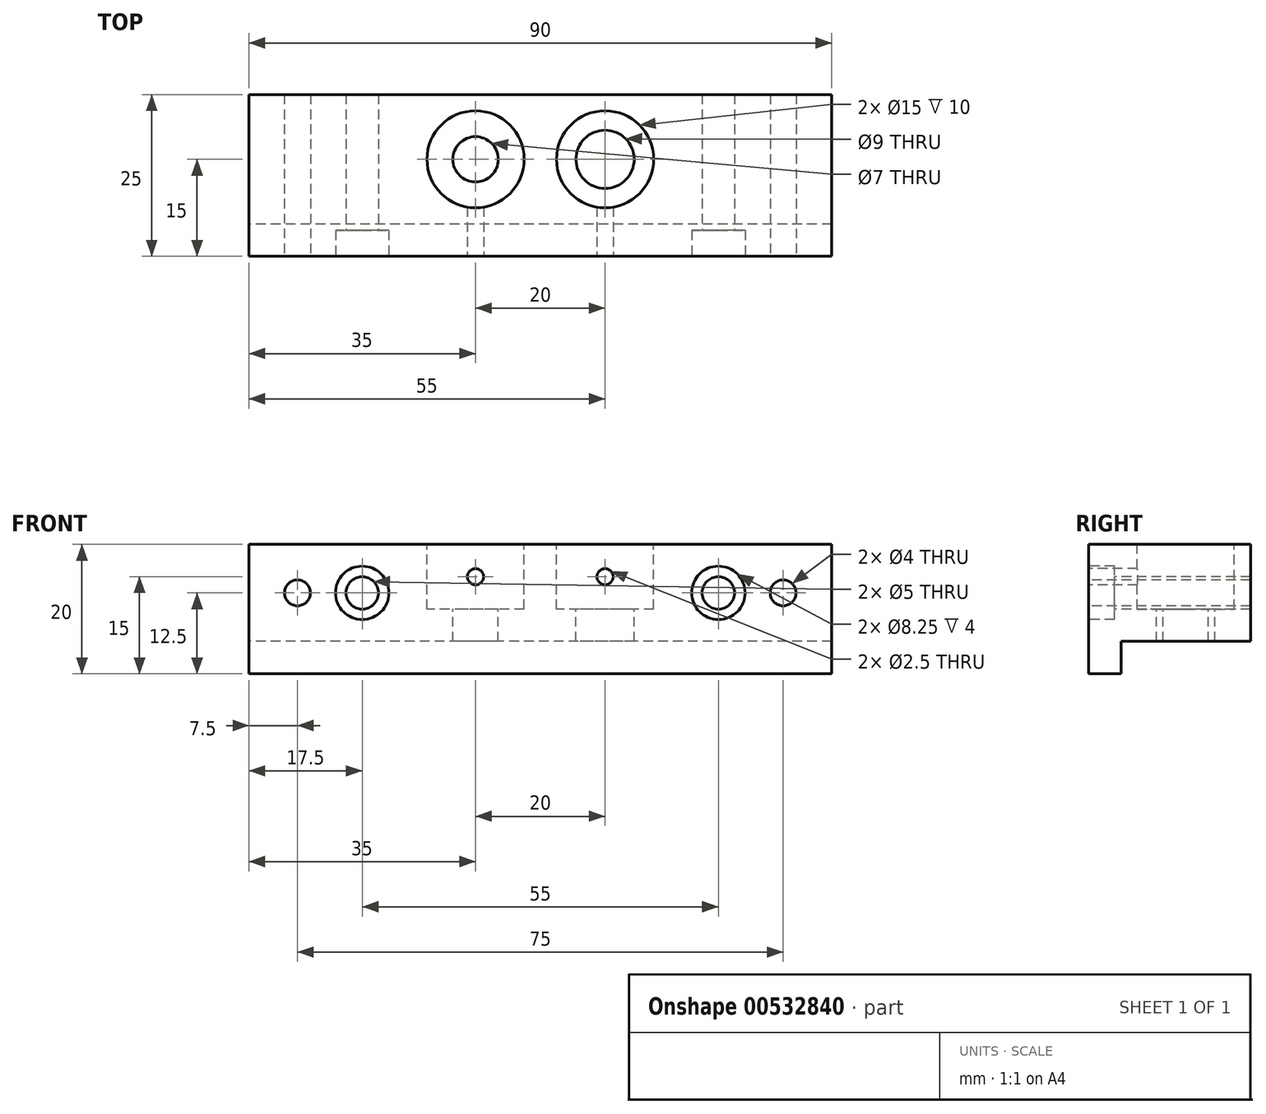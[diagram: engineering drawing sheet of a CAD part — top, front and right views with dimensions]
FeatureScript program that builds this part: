
annotation { "Feature Type Name" : "Feature", "Feature Type Description" : "" }
export const myFeature = defineFeature(function(context is Context, id is Id, definition is map)
    precondition{}
    {
        {
            var Q0;
            Q0=qCreatedBy(makeId("Right.planeOp"),FACE);
            var sketch = newSketch(context, id + "F0", { "sketchPlane" : qUnion([Q0])});
            skLineSegment(sketch, "E0", {"start": v(-25, 0) * mm, "end": v(-25, 20) * mm});
            skLineSegment(sketch, "E1", {"start": v(-25, 20) * mm, "end": v(0, 20) * mm});
            skLineSegment(sketch, "E2", {"start": v(0, 20) * mm, "end": v(0, 5) * mm});
            skLineSegment(sketch, "E3", {"start": v(0, 5) * mm, "end": v(-20, 5) * mm});
            skLineSegment(sketch, "E4", {"start": v(-20, 5) * mm, "end": v(-20, 0) * mm});
            skLineSegment(sketch, "E5", {"start": v(-20, 0) * mm, "end": v(-25, 0) * mm});
            skSolve(sketch);
        }
        {
            var Q0;
            Q0 = qSketchRegion(id + "F0", true);
            extrude(context, id + "F1", {"entities" : qUnion([Q0]), "endBound" : BoundingType.SYMMETRIC, "depth" : 90 * mm, "offsetDistance" : 25 * mm});
        }
        {
            var Q0;
            Q0=makeQuery(id+"F1.opExtrude","SWEPT_FACE",FACE,{"disambiguationData":[OSD([sQuery(id+"F0.wireOp",EDGE,"E0")])]});
            var sketch = newSketch(context, id + "F2", { "sketchPlane" : qUnion([Q0])});
            skPoint(sketch, "E6", {"position": v(-27.5, 12.5) * mm});
            skPoint(sketch, "E7", {"position": v(27.5, 12.5) * mm});
            skCircle(sketch, "E8", {"center": v(-37.5, 12.5) * mm, "radius": 2 * mm});
            skCircle(sketch, "E9", {"center": v(37.5, 12.5) * mm, "radius": 2 * mm});
            skSolve(sketch);
        }
        {
            var Q0;
            Q0=makeQuery(id+"F2.imprint","IMPRINT",FACE,{"disambiguationData":[TD([[makeQuery(id+"F2.imprint","IMPRINT",EDGE,{"derivedFrom":sQuery(id+"F2.wireOp",EDGE,"E8")}),1.0]])]});
            var Q1;
            Q1=makeQuery(id+"F2.imprint","IMPRINT",FACE,{"disambiguationData":[TD([[makeQuery(id+"F2.imprint","IMPRINT",EDGE,{"derivedFrom":sQuery(id+"F2.wireOp",EDGE,"E9")}),1.0]])]});
            extrude(context, id + "F3", {"entities" : qUnion([Q0, Q1]), "operationType" : NewBodyOperationType.REMOVE, "endBound" : BoundingType.THROUGH_ALL, "oppositeDirection" : true, "depth" : 25 * mm, "offsetDistance" : 25 * mm});
        }
        {
            var Q0;
            Q0=sQuery(id+"F2.wireOp",VERTEX,"E6");
            var Q1;
            Q1=sQuery(id+"F2.wireOp",VERTEX,"E7");
            var Q2;
            Q2=makeQuery(id+"F1.opExtrude","SWEPT_BODY",BODY,{"disambiguationData":[OSD([sQuery(id+"F0.wireOp",EDGE,"E0"),sQuery(id+"F0.wireOp",EDGE,"E1"),sQuery(id+"F0.wireOp",EDGE,"E2"),sQuery(id+"F0.wireOp",EDGE,"E3"),sQuery(id+"F0.wireOp",EDGE,"E4"),sQuery(id+"F0.wireOp",EDGE,"E5")])]});
            hole(context, id + "F4", {"style" : HoleStyle.C_BORE, "endStyle" : HoleEndStyle.THROUGH, "standardTappedOrClearance" : lookupTablePath({ "standard" : "ISO", "size" : "5", "type" : "Drilled" }), "standardBlindInLast" : lookupTablePath({ "standard" : "ISO", "size" : "5", "type" : "Drilled" }), "holeDiameter" : 5 * mm, "cBoreDiameter" : 8.25 * mm, "cBoreDepth" : 4 * mm, "isTappedThrough" : true, "tappedDepth" : 10.9 * mm, "tapClearance" : 3, "locations" : qUnion([Q0, Q1]), "scope" : qUnion([Q2])});
        }
        {
            var Q0;
            Q0=makeQuery(id+"F1.opExtrude","SWEPT_FACE",FACE,{"disambiguationData":[OSD([sQuery(id+"F0.wireOp",EDGE,"E1")])]});
            var sketch = newSketch(context, id + "F5", { "sketchPlane" : qUnion([Q0])});
            skCircle(sketch, "E10", {"center": v(-10, -10) * mm, "radius": 7.5 * mm});
            skCircle(sketch, "E11", {"center": v(-10, -10) * mm, "radius": 3.5 * mm});
            skCircle(sketch, "E12", {"center": v(10, -10) * mm, "radius": 7.5 * mm});
            skCircle(sketch, "E13", {"center": v(10, -10) * mm, "radius": 4.5 * mm});
            skSolve(sketch);
        }
        {
            var Q0;
            Q0=makeQuery(id+"F5.imprint","IMPRINT",FACE,{"disambiguationData":[TD([[makeQuery(id+"F5.imprint","IMPRINT",EDGE,{"derivedFrom":sQuery(id+"F5.wireOp",EDGE,"E11")}),1.0]])]});
            var Q1;
            Q1=makeQuery(id+"F5.imprint","IMPRINT",FACE,{"disambiguationData":[TD([[makeQuery(id+"F5.imprint","IMPRINT",EDGE,{"derivedFrom":sQuery(id+"F5.wireOp",EDGE,"E13")}),1.0]])]});
            extrude(context, id + "F6", {"entities" : qUnion([Q0, Q1]), "operationType" : NewBodyOperationType.REMOVE, "endBound" : BoundingType.THROUGH_ALL, "oppositeDirection" : true, "depth" : 25 * mm, "offsetDistance" : 25 * mm});
        }
        {
            var Q0;
            Q0=makeQuery(id+"F5.imprint","IMPRINT",FACE,{"disambiguationData":[TD([[makeQuery(id+"F5.imprint","IMPRINT",EDGE,{"derivedFrom":sQuery(id+"F5.wireOp",EDGE,"E10")}),1.0]])]});
            var Q1;
            Q1=makeQuery(id+"F5.imprint","IMPRINT",FACE,{"disambiguationData":[TD([[makeQuery(id+"F5.imprint","IMPRINT",EDGE,{"derivedFrom":sQuery(id+"F5.wireOp",EDGE,"E12")}),1.0]])]});
            extrude(context, id + "F7", {"entities" : qUnion([Q0, Q1]), "operationType" : NewBodyOperationType.REMOVE, "oppositeDirection" : true, "depth" : 10 * mm, "offsetDistance" : 25 * mm});
        }
        {
            var Q0;
            Q0=makeQuery(id+"F1.opExtrude","SWEPT_FACE",FACE,{"disambiguationData":[OSD([sQuery(id+"F0.wireOp",EDGE,"E0")])]});
            var sketch = newSketch(context, id + "F8", { "sketchPlane" : qUnion([Q0])});
            skPoint(sketch, "E14", {"position": v(-10, 15) * mm});
            skPoint(sketch, "E15", {"position": v(10, 15) * mm});
            skSolve(sketch);
        }
        {
            var Q0;
            Q0=sQuery(id+"F8.wireOp",VERTEX,"E14");
            var Q1;
            Q1=sQuery(id+"F8.wireOp",VERTEX,"E15");
            var Q2;
            Q2=makeQuery(id+"F1.opExtrude","SWEPT_BODY",BODY,{"disambiguationData":[OSD([sQuery(id+"F0.wireOp",EDGE,"E0"),sQuery(id+"F0.wireOp",EDGE,"E1"),sQuery(id+"F0.wireOp",EDGE,"E2"),sQuery(id+"F0.wireOp",EDGE,"E3"),sQuery(id+"F0.wireOp",EDGE,"E4"),sQuery(id+"F0.wireOp",EDGE,"E5")])]});
            hole(context, id + "F9", {"style" : HoleStyle.SIMPLE, "endStyle" : HoleEndStyle.BLIND, "standardTappedOrClearance" : lookupTablePath({ "standard" : "ISO", "engagement" : "75%", "pitch" : "0.5 mm", "size" : "M3", "type" : "Tapped" }), "standardBlindInLast" : lookupTablePath({ "standard" : "ISO", "engagement" : "75%", "pitch" : "0.5 mm", "size" : "M3", "type" : "Tapped" }), "holeDiameter" : 2.5 * mm, "showTappedDepth" : true, "holeDepth" : 12.4 * mm, "isTappedThrough" : true, "tappedDepth" : 10.9 * mm, "tapClearance" : 3, "startFromSketch" : true, "locations" : qUnion([Q0, Q1]), "scope" : qUnion([Q2]), "majorDiameter" : 3 * mm});
        }
    });
